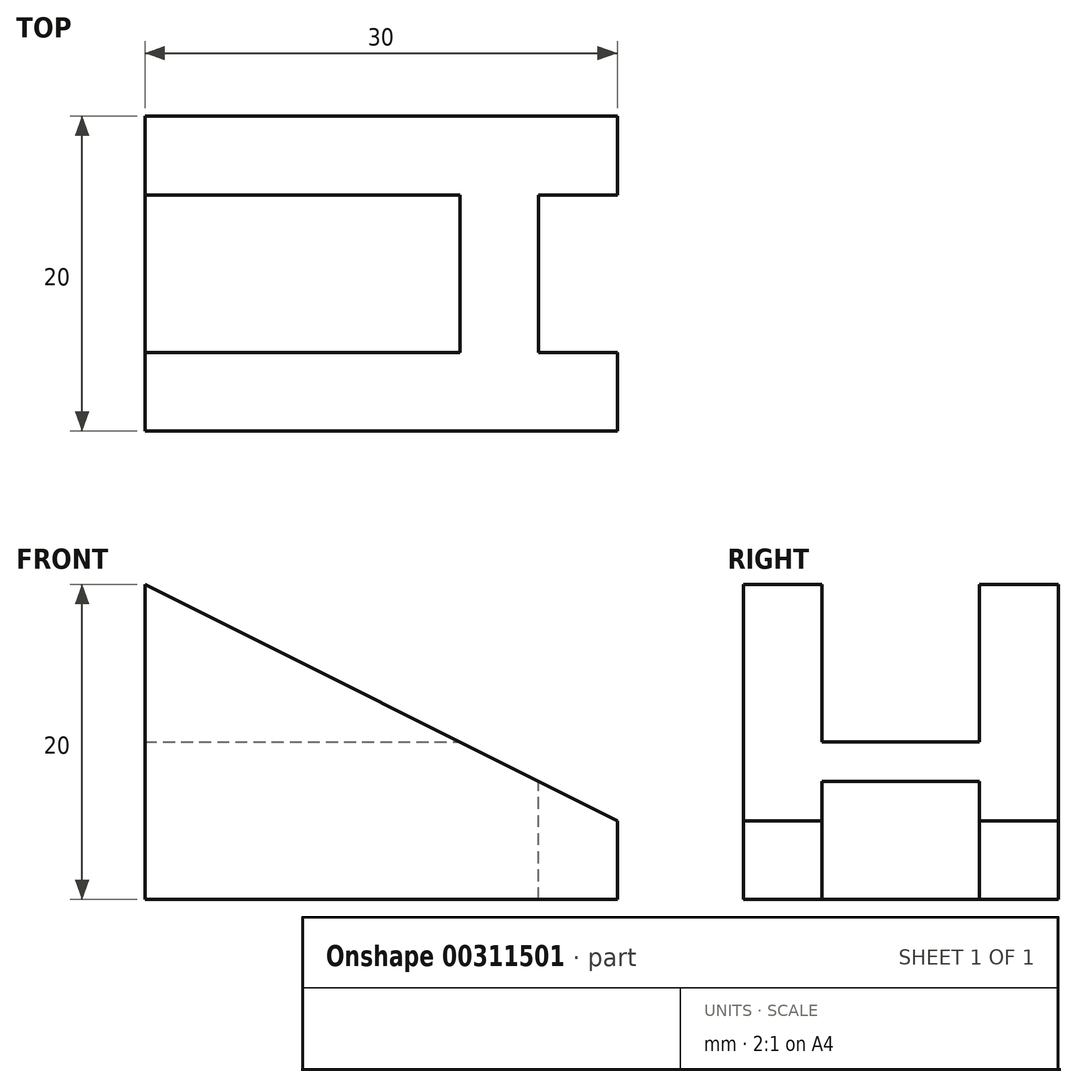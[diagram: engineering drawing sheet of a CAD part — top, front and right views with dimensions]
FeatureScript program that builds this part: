
annotation { "Feature Type Name" : "Feature", "Feature Type Description" : "" }
export const myFeature = defineFeature(function(context is Context, id is Id, definition is map)
    precondition{}
    {
        {
            var Q0;
            Q0=qCreatedBy(makeId("Front.planeOp"),FACE);
            var sketch = newSketch(context, id + "F0", { "sketchPlane" : qUnion([Q0])});
            skLineSegment(sketch, "E0", {"start": v(0, 0) * mm, "end": v(0, 20) * mm});
            skLineSegment(sketch, "E1", {"start": v(0, 0) * mm, "end": v(30, 0) * mm});
            skLineSegment(sketch, "E2", {"start": v(30, 0) * mm, "end": v(30, 5) * mm});
            skLineSegment(sketch, "E3", {"start": v(30, 5) * mm, "end": v(0, 20) * mm});
            skSolve(sketch);
        }
        {
            var Q0;
            Q0 = qSketchRegion(id + "F0", true);
            extrude(context, id + "F1", {"entities" : qUnion([Q0]), "depth" : 5 * mm});
        }
        {
            var Q0;
            Q0=makeQuery(id+"F1.opExtrude","CAP_FACE",FACE,{"disambiguationData":[OSD([sQuery(id+"F0.wireOp",EDGE,"E0"),sQuery(id+"F0.wireOp",EDGE,"E1"),sQuery(id+"F0.wireOp",EDGE,"E2"),sQuery(id+"F0.wireOp",EDGE,"E3")])],"isStart":false});
            var sketch = newSketch(context, id + "F2", { "sketchPlane" : qUnion([Q0])});
            skLineSegment(sketch, "E4", {"start": v(0, 0) * mm, "end": v(0, 10) * mm});
            skLineSegment(sketch, "E5", {"start": v(0, 0) * mm, "end": v(25, 0) * mm});
            skLineSegment(sketch, "E6", {"start": v(0, 10) * mm, "end": v(20, 10) * mm});
            skLineSegment(sketch, "E7", {"start": v(25, 0) * mm, "end": v(25, 7.5) * mm});
            skLineSegment(sketch, "E8", {"start": v(25, 7.5) * mm, "end": v(20, 10) * mm});
            skSolve(sketch);
        }
        {
            var Q0;
            Q0 = qSketchRegion(id + "F2", true);
            extrude(context, id + "F3", {"entities" : qUnion([Q0]), "operationType" : NewBodyOperationType.ADD, "depth" : 10 * mm});
        }
        {
            var Q0;
            Q0=makeQuery(id+"F3.opExtrude","CAP_FACE",FACE,{"disambiguationData":[OSD([sQuery(id+"F2.wireOp",EDGE,"E4"),sQuery(id+"F2.wireOp",EDGE,"E5"),sQuery(id+"F2.wireOp",EDGE,"E6"),sQuery(id+"F2.wireOp",EDGE,"E7"),sQuery(id+"F2.wireOp",EDGE,"E8")])],"isStart":false});
            var sketch = newSketch(context, id + "F4", { "sketchPlane" : qUnion([Q0])});
            skLineSegment(sketch, "E9", {"start": v(0, 0) * mm, "end": v(0, 20) * mm});
            skLineSegment(sketch, "E10", {"start": v(0, 0) * mm, "end": v(30, 0) * mm});
            skLineSegment(sketch, "E11", {"start": v(30, 0) * mm, "end": v(30, 5) * mm});
            skLineSegment(sketch, "E12", {"start": v(30, 5) * mm, "end": v(0, 20) * mm});
            skSolve(sketch);
        }
        {
            var Q0;
            Q0 = qSketchRegion(id + "F4", true);
            extrude(context, id + "F5", {"entities" : qUnion([Q0]), "operationType" : NewBodyOperationType.ADD, "depth" : 5 * mm});
        }
    });
